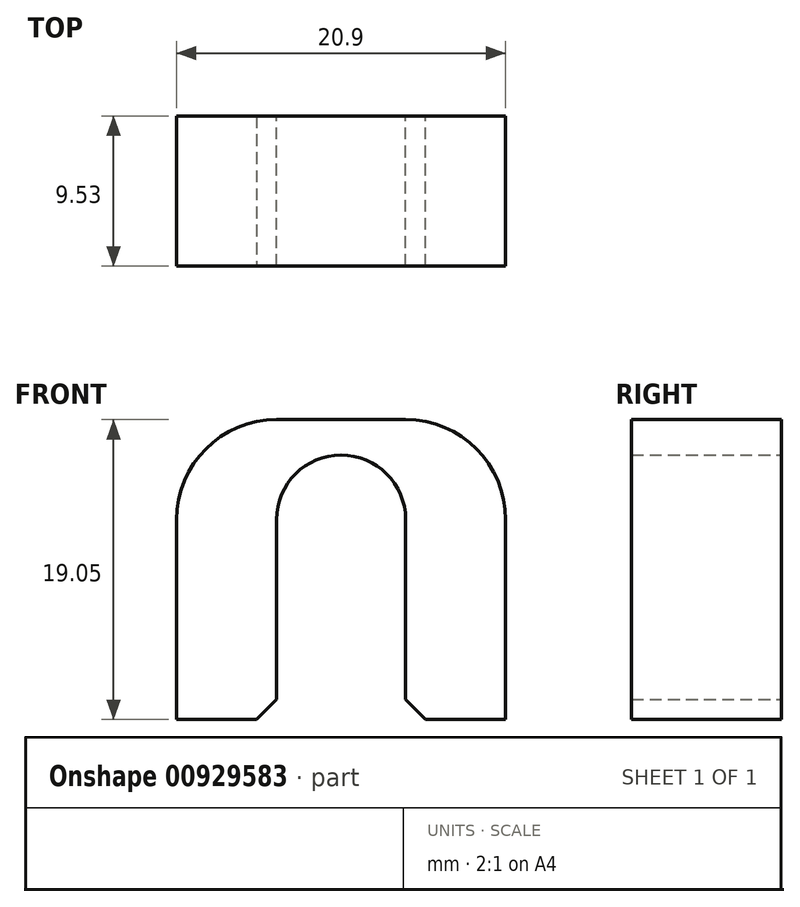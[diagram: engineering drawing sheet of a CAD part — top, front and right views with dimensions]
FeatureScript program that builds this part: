
annotation { "Feature Type Name" : "Feature", "Feature Type Description" : "" }
export const myFeature = defineFeature(function(context is Context, id is Id, definition is map)
    precondition{}
    {
        {
            var Q0;
            Q0=qCreatedBy(makeId("Front.planeOp"),FACE);
            var sketch = newSketch(context, id + "F0", { "sketchPlane" : qUnion([Q0])});
            skLineSegment(sketch, "E0", {"start": v(-4.1, 0) * mm, "end": v(-4.1, -12.7) * mm});
            skLineSegment(sketch, "E1", {"start": v(-10.45, -12.7) * mm, "end": v(-4.1, -12.7) * mm});
            skPoint(sketch, "E2", {"position": v(0, 4.1) * mm});
            skArc(sketch, "E3", {"start": v(0, 4.1) * mm, "mid": v(-2.9, 2.9) * mm, "end": v(-4.1, 0) * mm});
            skLineSegment(sketch, "E4", {"start": v(-10.45, -12.7) * mm, "end": v(-10.45, 6.35) * mm});
            skLineSegment(sketch, "E5", {"start": v(-10.45, 6.35) * mm, "end": v(0, 6.35) * mm});
            skLineSegment(sketch, "E6", {"start": v(0, 6.35) * mm, "end": v(0, 4.1) * mm});
            skLineSegment(sketch, "E7", {"start": v(0, 0) * mm, "end": v(0, -12.7) * mm, "construction": true});
            skArc(sketch, "E8.MirrorCS", {"start": v(0, 4.1) * mm, "mid": v(2.9, 2.9) * mm, "end": v(4.1, 0) * mm});
            skLineSegment(sketch, "E9.MirrorCS", {"start": v(4.1, 0) * mm, "end": v(4.1, -12.7) * mm});
            skLineSegment(sketch, "E10.MirrorCS", {"start": v(10.45, -12.7) * mm, "end": v(4.1, -12.7) * mm});
            skLineSegment(sketch, "E11.MirrorCS", {"start": v(10.45, -12.7) * mm, "end": v(10.45, 6.35) * mm});
            skLineSegment(sketch, "E12.MirrorCS", {"start": v(10.45, 6.35) * mm, "end": v(0, 6.35) * mm});
            skSolve(sketch);
        }
        {
            var Q0;
            Q0=makeQuery(id+"F0.imprint","IMPRINT",FACE,{"disambiguationData":[TD([[makeQuery(id+"F0.imprint","IMPRINT",EDGE,{"derivedFrom":sQuery(id+"F0.wireOp",EDGE,"E0")}),-1.0]])]});
            var Q1;
            Q1=makeQuery(id+"F0.imprint","IMPRINT",FACE,{"disambiguationData":[TD([[makeQuery(id+"F0.imprint","IMPRINT",EDGE,{"derivedFrom":sQuery(id+"F0.wireOp",EDGE,"E6")}),1.0]])]});
            extrude(context, id + "F1", {"entities" : qUnion([Q0, Q1]), "depth" : 9.52 * mm, "offsetDistance" : 25.4 * mm});
        }
        {
            var Q0;
            Q0=makeQuery(id+"F1.opExtrude","SWEPT_EDGE",EDGE,{"disambiguationData":[OSD([sQuery(id+"F0.wireOp",EDGE,"E4"),sQuery(id+"F0.wireOp",EDGE,"E5")])]});
            var Q1;
            Q1=makeQuery(id+"F1.opExtrude","SWEPT_EDGE",EDGE,{"disambiguationData":[OSD([sQuery(id+"F0.wireOp",EDGE,"E11.MirrorCS"),sQuery(id+"F0.wireOp",EDGE,"E12.MirrorCS")])]});
            fillet(context, id + "F2", {"entities" : qUnion([Q0, Q1]), "radius" : 6.35 * mm, "tangentPropagation" : true, "allowEdgeOverflow" : false});
        }
        {
            var Q0;
            Q0=makeQuery(id+"F1.opExtrude","SWEPT_EDGE",EDGE,{"disambiguationData":[OSD([sQuery(id+"F0.wireOp",EDGE,"E0"),sQuery(id+"F0.wireOp",EDGE,"E1")])]});
            var Q1;
            Q1=makeQuery(id+"F1.opExtrude","SWEPT_EDGE",EDGE,{"disambiguationData":[OSD([sQuery(id+"F0.wireOp",EDGE,"E9.MirrorCS"),sQuery(id+"F0.wireOp",EDGE,"E10.MirrorCS")])]});
            chamfer(context, id + "F3", {"entities" : qUnion([Q0, Q1]), "width" : 1.27 * mm, "tangentPropagation" : true});
        }
    });
